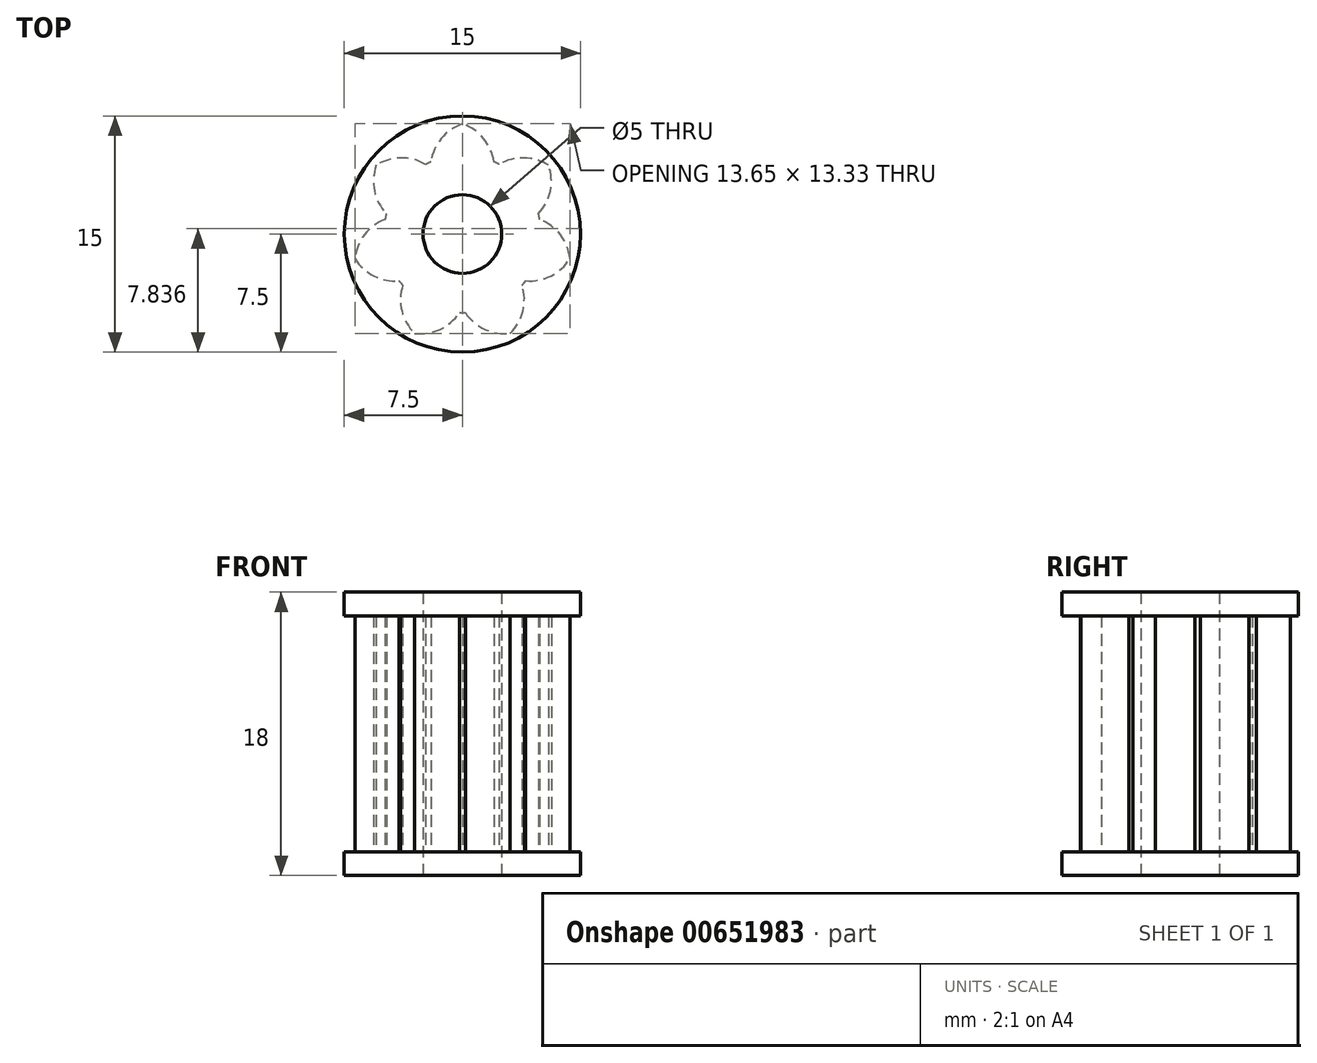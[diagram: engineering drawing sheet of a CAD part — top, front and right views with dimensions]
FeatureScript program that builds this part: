
annotation { "Feature Type Name" : "Feature", "Feature Type Description" : "" }
export const myFeature = defineFeature(function(context is Context, id is Id, definition is map)
    precondition{}
    {
        {
            var Q0;
            Q0=qCreatedBy(makeId("Top.planeOp"),FACE);
            var sketch = newSketch(context, id + "F0", { "sketchPlane" : qUnion([Q0])});
            skCircle(sketch, "E0", {"center": v(0, 0) * mm, "radius": 2.5 * mm});
            skArc(sketch, "E1", {"start": v(-2, 4.58) * mm, "mid": v(-2.17, 4.5) * mm, "end": v(-2.34, 4.42) * mm});
            skArc(sketch, "E2", {"start": v(0, 7) * mm, "mid": v(-1.34, 6.07) * mm, "end": v(-2, 4.58) * mm});
            skArc(sketch, "E3", {"start": v(2, 4.58) * mm, "mid": v(1.34, 6.07) * mm, "end": v(0, 7) * mm});
            skArc(sketch, "E4.1.0", {"start": v(-5.47, 4.36) * mm, "mid": v(-5.58, 2.74) * mm, "end": v(-4.83, 1.3) * mm});
            skArc(sketch, "E4.1.1", {"start": v(-2.34, 4.42) * mm, "mid": v(-3.91, 4.84) * mm, "end": v(-5.47, 4.36) * mm});
            skArc(sketch, "E4.2.0", {"start": v(-6.82, -1.56) * mm, "mid": v(-5.62, -2.66) * mm, "end": v(-4.02, -2.97) * mm});
            skArc(sketch, "E4.2.1", {"start": v(-4.91, 0.93) * mm, "mid": v(-6.22, -0.04) * mm, "end": v(-6.82, -1.56) * mm});
            skArc(sketch, "E4.3.0", {"start": v(-3.04, -6.3) * mm, "mid": v(-1.43, -6.05) * mm, "end": v(-0.19, -5) * mm});
            skArc(sketch, "E4.3.1", {"start": v(-3.8, -3.26) * mm, "mid": v(-3.84, -4.9) * mm, "end": v(-3.04, -6.3) * mm});
            skArc(sketch, "E4.4.0", {"start": v(3.04, -6.3) * mm, "mid": v(3.84, -4.9) * mm, "end": v(3.8, -3.26) * mm});
            skArc(sketch, "E4.4.1", {"start": v(0.19, -5) * mm, "mid": v(1.43, -6.05) * mm, "end": v(3.04, -6.3) * mm});
            skArc(sketch, "E4.5.0", {"start": v(6.82, -1.56) * mm, "mid": v(6.22, -0.04) * mm, "end": v(4.91, 0.93) * mm});
            skArc(sketch, "E4.5.1", {"start": v(4.02, -2.97) * mm, "mid": v(5.62, -2.66) * mm, "end": v(6.82, -1.56) * mm});
            skArc(sketch, "E4.6.0", {"start": v(5.47, 4.36) * mm, "mid": v(3.91, 4.84) * mm, "end": v(2.34, 4.42) * mm});
            skArc(sketch, "E4.6.1", {"start": v(4.83, 1.3) * mm, "mid": v(5.58, 2.74) * mm, "end": v(5.47, 4.36) * mm});
            skArc(sketch, "E5.trimOffspring", {"start": v(-4.83, 1.3) * mm, "mid": v(-4.87, 1.11) * mm, "end": v(-4.91, 0.93) * mm});
            skArc(sketch, "E6.trimOffspring", {"start": v(-4.02, -2.97) * mm, "mid": v(-3.9, -3.12) * mm, "end": v(-3.8, -3.26) * mm});
            skArc(sketch, "E7.trimOffspring", {"start": v(-0.19, -5) * mm, "mid": v(0, -5) * mm, "end": v(0.19, -5) * mm});
            skArc(sketch, "E8.trimOffspring", {"start": v(3.8, -3.26) * mm, "mid": v(3.9, -3.12) * mm, "end": v(4.02, -2.97) * mm});
            skArc(sketch, "E9.trimOffspring", {"start": v(4.91, 0.93) * mm, "mid": v(4.87, 1.11) * mm, "end": v(4.83, 1.3) * mm});
            skArc(sketch, "E10.trimOffspring", {"start": v(2.34, 4.42) * mm, "mid": v(2.17, 4.5) * mm, "end": v(2, 4.58) * mm});
            skSolve(sketch);
        }
        {
            var Q0;
            Q0 = qSketchRegion(id + "F0", true);
            extrude(context, id + "F1", {"entities" : qUnion([Q0]), "depth" : 15 * mm, "offsetDistance" : 25 * mm});
        }
        {
            var Q0;
            Q0=makeQuery(id+"F1.opExtrude","CAP_FACE",FACE,{"disambiguationData":[OSD([sQuery(id+"F0.wireOp",EDGE,"E0"),sQuery(id+"F0.wireOp",EDGE,"E1"),sQuery(id+"F0.wireOp",EDGE,"E2"),sQuery(id+"F0.wireOp",EDGE,"E3"),sQuery(id+"F0.wireOp",EDGE,"E4.1.0"),sQuery(id+"F0.wireOp",EDGE,"E4.1.1"),sQuery(id+"F0.wireOp",EDGE,"E4.2.0"),sQuery(id+"F0.wireOp",EDGE,"E4.2.1"),sQuery(id+"F0.wireOp",EDGE,"E4.3.0"),sQuery(id+"F0.wireOp",EDGE,"E4.3.1"),sQuery(id+"F0.wireOp",EDGE,"E4.4.0"),sQuery(id+"F0.wireOp",EDGE,"E4.4.1"),sQuery(id+"F0.wireOp",EDGE,"E4.5.0"),sQuery(id+"F0.wireOp",EDGE,"E4.5.1"),sQuery(id+"F0.wireOp",EDGE,"E4.6.0"),sQuery(id+"F0.wireOp",EDGE,"E4.6.1"),sQuery(id+"F0.wireOp",EDGE,"E5.trimOffspring"),sQuery(id+"F0.wireOp",EDGE,"E6.trimOffspring"),sQuery(id+"F0.wireOp",EDGE,"E7.trimOffspring"),sQuery(id+"F0.wireOp",EDGE,"E8.trimOffspring"),sQuery(id+"F0.wireOp",EDGE,"E9.trimOffspring"),sQuery(id+"F0.wireOp",EDGE,"E10.trimOffspring")])],"isStart":false});
            var sketch = newSketch(context, id + "F2", { "sketchPlane" : qUnion([Q0])});
            skCircle(sketch, "E11", {"center": v(0, 0) * mm, "radius": 7.5 * mm});
            skSolve(sketch);
        }
        {
            var Q0;
            Q0=makeQuery(id+"F2.imprint","IMPRINT",FACE,{"disambiguationData":[TD([[makeQuery(id+"F2.imprint","IMPRINT",EDGE,{"derivedFrom":makeQuery(id+"F1.opExtrude","CAP_EDGE",EDGE,{"disambiguationData":[OSD([sQuery(id+"F0.wireOp",EDGE,"E0")])],"isStart":false})}),-1.0]])]});
            var Q1;
            Q1=makeQuery(id+"F2.imprint","IMPRINT",FACE,{"disambiguationData":[TD([[makeQuery(id+"F2.imprint","IMPRINT",EDGE,{"derivedFrom":sQuery(id+"F2.wireOp",EDGE,"E11")}),1.0]])]});
            extrude(context, id + "F3", {"entities" : qUnion([Q0, Q1]), "operationType" : NewBodyOperationType.ADD, "depth" : 1.5 * mm, "offsetDistance" : 25 * mm});
        }
        {
            var Q0;
            Q0=makeQuery(id+"F1.opExtrude","CAP_FACE",FACE,{"disambiguationData":[OSD([sQuery(id+"F0.wireOp",EDGE,"E0"),sQuery(id+"F0.wireOp",EDGE,"E1"),sQuery(id+"F0.wireOp",EDGE,"E2"),sQuery(id+"F0.wireOp",EDGE,"E3"),sQuery(id+"F0.wireOp",EDGE,"E4.1.0"),sQuery(id+"F0.wireOp",EDGE,"E4.1.1"),sQuery(id+"F0.wireOp",EDGE,"E4.2.0"),sQuery(id+"F0.wireOp",EDGE,"E4.2.1"),sQuery(id+"F0.wireOp",EDGE,"E4.3.0"),sQuery(id+"F0.wireOp",EDGE,"E4.3.1"),sQuery(id+"F0.wireOp",EDGE,"E4.4.0"),sQuery(id+"F0.wireOp",EDGE,"E4.4.1"),sQuery(id+"F0.wireOp",EDGE,"E4.5.0"),sQuery(id+"F0.wireOp",EDGE,"E4.5.1"),sQuery(id+"F0.wireOp",EDGE,"E4.6.0"),sQuery(id+"F0.wireOp",EDGE,"E4.6.1"),sQuery(id+"F0.wireOp",EDGE,"E5.trimOffspring"),sQuery(id+"F0.wireOp",EDGE,"E6.trimOffspring"),sQuery(id+"F0.wireOp",EDGE,"E7.trimOffspring"),sQuery(id+"F0.wireOp",EDGE,"E8.trimOffspring"),sQuery(id+"F0.wireOp",EDGE,"E9.trimOffspring"),sQuery(id+"F0.wireOp",EDGE,"E10.trimOffspring")])],"isStart":true});
            var sketch = newSketch(context, id + "F4", { "sketchPlane" : qUnion([Q0])});
            skCircle(sketch, "E12", {"center": v(0, 0) * mm, "radius": 7.5 * mm});
            skSolve(sketch);
        }
        {
            var Q0;
            Q0=makeQuery(id+"F4.imprint","IMPRINT",FACE,{"disambiguationData":[TD([[makeQuery(id+"F4.imprint","IMPRINT",EDGE,{"derivedFrom":sQuery(id+"F4.wireOp",EDGE,"E12")}),1.0]])]});
            var Q1;
            Q1=makeQuery(id+"F4.imprint","IMPRINT",FACE,{"disambiguationData":[TD([[makeQuery(id+"F4.imprint","IMPRINT",EDGE,{"derivedFrom":makeQuery(id+"F1.opExtrude","CAP_EDGE",EDGE,{"disambiguationData":[OSD([sQuery(id+"F0.wireOp",EDGE,"E0")])],"isStart":true})}),1.0]])]});
            extrude(context, id + "F5", {"entities" : qUnion([Q0, Q1]), "operationType" : NewBodyOperationType.ADD, "depth" : 1.5 * mm, "offsetDistance" : 25 * mm});
        }
    });
